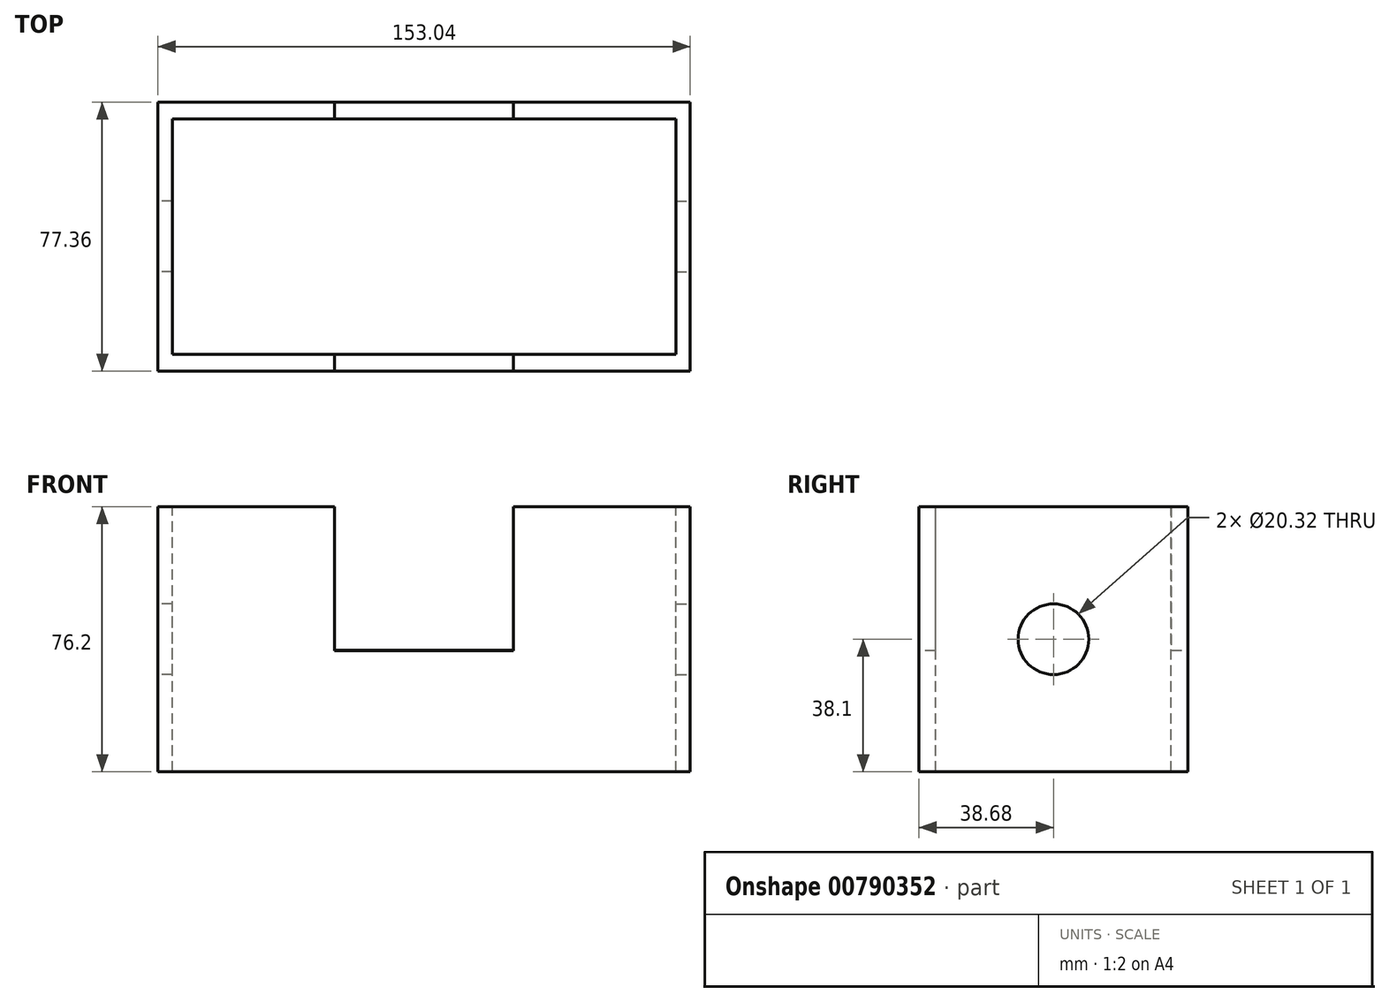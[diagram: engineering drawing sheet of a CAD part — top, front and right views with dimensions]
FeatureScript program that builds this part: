
annotation { "Feature Type Name" : "Feature", "Feature Type Description" : "" }
export const myFeature = defineFeature(function(context is Context, id is Id, definition is map)
    precondition{}
    {
        {
            var Q0;
            Q0=qCreatedBy(makeId("Top.planeOp"),FACE);
            var sketch = newSketch(context, id + "F0", { "sketchPlane" : qUnion([Q0])});
            skLineSegment(sketch, "E0.bottom", {"start": v(76.52, -38.68) * mm, "end": v(-76.52, -38.68) * mm});
            skLineSegment(sketch, "E0.top", {"start": v(76.52, 38.68) * mm, "end": v(-76.52, 38.68) * mm});
            skLineSegment(sketch, "E0.left", {"start": v(76.52, -38.68) * mm, "end": v(76.52, 38.68) * mm});
            skLineSegment(sketch, "E0.right", {"start": v(-76.52, -38.68) * mm, "end": v(-76.52, 38.68) * mm});
            skPoint(sketch, "E0.middle", {"position": v(0, 0) * mm});
            skSolve(sketch);
        }
        {
            var Q0;
            Q0=makeQuery(id+"F0.imprint","IMPRINT",FACE,{"disambiguationData":[TD([[makeQuery(id+"F0.imprint","IMPRINT",EDGE,{"derivedFrom":sQuery(id+"F0.wireOp",EDGE,"E0.bottom")}),-1.0]])]});
            extrude(context, id + "F1", {"entities" : qUnion([Q0]), "depth" : 76.2 * mm, "offsetDistance" : 25.4 * mm});
        }
        {
            var Q0;
            Q0=makeQuery(id+"F1.opExtrude","CAP_FACE",FACE,{"disambiguationData":[OSD([sQuery(id+"F0.wireOp",EDGE,"E0.bottom"),sQuery(id+"F0.wireOp",EDGE,"E0.top"),sQuery(id+"F0.wireOp",EDGE,"E0.left"),sQuery(id+"F0.wireOp",EDGE,"E0.right")])],"isStart":false});
            var sketch = newSketch(context, id + "F2", { "sketchPlane" : qUnion([Q0])});
            skLineSegment(sketch, "E1.bottom", {"start": v(72.42, -33.86) * mm, "end": v(-72.42, -33.86) * mm});
            skLineSegment(sketch, "E1.top", {"start": v(72.42, 33.86) * mm, "end": v(-72.42, 33.86) * mm});
            skLineSegment(sketch, "E1.left", {"start": v(72.42, -33.86) * mm, "end": v(72.42, 33.86) * mm});
            skLineSegment(sketch, "E1.right", {"start": v(-72.42, -33.86) * mm, "end": v(-72.42, 33.86) * mm});
            skPoint(sketch, "E1.middle", {"position": v(0, 0) * mm});
            skSolve(sketch);
        }
        {
            var Q0;
            Q0=makeQuery(id+"F2.imprint","IMPRINT",FACE,{"disambiguationData":[TD([[makeQuery(id+"F2.imprint","IMPRINT",EDGE,{"derivedFrom":sQuery(id+"F2.wireOp",EDGE,"E1.bottom")}),-1.0]])]});
            extrude(context, id + "F3", {"entities" : qUnion([Q0]), "operationType" : NewBodyOperationType.REMOVE, "oppositeDirection" : true, "depth" : 76.2 * mm, "offsetDistance" : 25.4 * mm});
        }
        {
            var Q0;
            Q0=makeQuery(id+"F1.opExtrude","SWEPT_FACE",FACE,{"disambiguationData":[OSD([sQuery(id+"F0.wireOp",EDGE,"E0.bottom")])]});
            var sketch = newSketch(context, id + "F4", { "sketchPlane" : qUnion([Q0])});
            skLineSegment(sketch, "E2", {"start": v(-76.52, 76.2) * mm, "end": v(-25.72, 76.2) * mm});
            skLineSegment(sketch, "E3", {"start": v(76.52, 76.2) * mm, "end": v(25.72, 76.2) * mm});
            skLineSegment(sketch, "E4.bottom", {"start": v(25.72, 76.2) * mm, "end": v(-25.72, 76.2) * mm});
            skLineSegment(sketch, "E4.top", {"start": v(25.72, 34.8) * mm, "end": v(-25.72, 34.8) * mm});
            skLineSegment(sketch, "E4.left", {"start": v(25.72, 76.2) * mm, "end": v(25.72, 34.8) * mm});
            skLineSegment(sketch, "E4.right", {"start": v(-25.72, 76.2) * mm, "end": v(-25.72, 34.8) * mm});
            skSolve(sketch);
        }
        {
            var Q0;
            Q0=makeQuery(id+"F4.imprint","IMPRINT",FACE,{"disambiguationData":[TD([[makeQuery(id+"F4.imprint","IMPRINT",EDGE,{"derivedFrom":sQuery(id+"F4.wireOp",EDGE,"E4.bottom")}),1.0]])]});
            extrude(context, id + "F5", {"entities" : qUnion([Q0]), "operationType" : NewBodyOperationType.REMOVE, "oppositeDirection" : true, "depth" : 25.4 * mm, "offsetDistance" : 25.4 * mm});
        }
        {
            var Q0;
            Q0=makeQuery(id+"F1.opExtrude","SWEPT_FACE",FACE,{"disambiguationData":[OSD([sQuery(id+"F0.wireOp",EDGE,"E0.top")])]});
            var sketch = newSketch(context, id + "F6", { "sketchPlane" : qUnion([Q0])});
            skLineSegment(sketch, "E5", {"start": v(-76.52, 76.2) * mm, "end": v(-25.72, 76.2) * mm});
            skLineSegment(sketch, "E6", {"start": v(76.52, 76.2) * mm, "end": v(25.72, 76.2) * mm});
            skLineSegment(sketch, "E7.bottom", {"start": v(-25.72, 76.2) * mm, "end": v(25.72, 76.2) * mm});
            skLineSegment(sketch, "E7.top", {"start": v(-25.72, 34.9) * mm, "end": v(25.72, 34.9) * mm});
            skLineSegment(sketch, "E7.left", {"start": v(-25.72, 76.2) * mm, "end": v(-25.72, 34.9) * mm});
            skLineSegment(sketch, "E7.right", {"start": v(25.72, 76.2) * mm, "end": v(25.72, 34.9) * mm});
            skSolve(sketch);
        }
        {
            var Q0;
            Q0 = qSketchRegion(id + "F6", true);
            extrude(context, id + "F7", {"entities" : qUnion([Q0]), "operationType" : NewBodyOperationType.REMOVE, "oppositeDirection" : true, "depth" : 25.4 * mm, "offsetDistance" : 25.4 * mm});
        }
        {
            var Q0;
            Q0=makeQuery(id+"F1.opExtrude","SWEPT_FACE",FACE,{"disambiguationData":[OSD([sQuery(id+"F0.wireOp",EDGE,"E0.left")])]});
            var sketch = newSketch(context, id + "F8", { "sketchPlane" : qUnion([Q0])});
            skLineSegment(sketch, "E8", {"start": v(-38.68, 76.2) * mm, "end": v(38.68, 76.2) * mm});
            skCircle(sketch, "E9", {"center": v(0, 38.1) * mm, "radius": 10.16 * mm});
            skPoint(sketch, "E10.orphan", {"position": v(0, 76.2) * mm});
            skSolve(sketch);
        }
        {
            var Q0;
            Q0=makeQuery(id+"F8.imprint","IMPRINT",FACE,{"disambiguationData":[TD([[makeQuery(id+"F8.imprint","IMPRINT",EDGE,{"derivedFrom":sQuery(id+"F8.wireOp",EDGE,"E9")}),1.0]])]});
            extrude(context, id + "F9", {"entities" : qUnion([Q0]), "operationType" : NewBodyOperationType.REMOVE, "oppositeDirection" : true, "depth" : 25.4 * mm, "offsetDistance" : 25.4 * mm});
        }
        {
            var Q0;
            Q0=makeQuery(id+"F1.opExtrude","SWEPT_FACE",FACE,{"disambiguationData":[OSD([sQuery(id+"F0.wireOp",EDGE,"E0.right")])]});
            var sketch = newSketch(context, id + "F10", { "sketchPlane" : qUnion([Q0])});
            skCircle(sketch, "E11", {"center": v(0, 38.1) * mm, "radius": 10.16 * mm});
            skSolve(sketch);
        }
        {
            var Q0;
            Q0=makeQuery(id+"F10.imprint","IMPRINT",FACE,{"disambiguationData":[TD([[makeQuery(id+"F10.imprint","IMPRINT",EDGE,{"derivedFrom":sQuery(id+"F10.wireOp",EDGE,"E11")}),1.0]])]});
            extrude(context, id + "F11", {"entities" : qUnion([Q0]), "operationType" : NewBodyOperationType.REMOVE, "oppositeDirection" : true, "depth" : 25.4 * mm, "offsetDistance" : 25.4 * mm});
        }
    });
